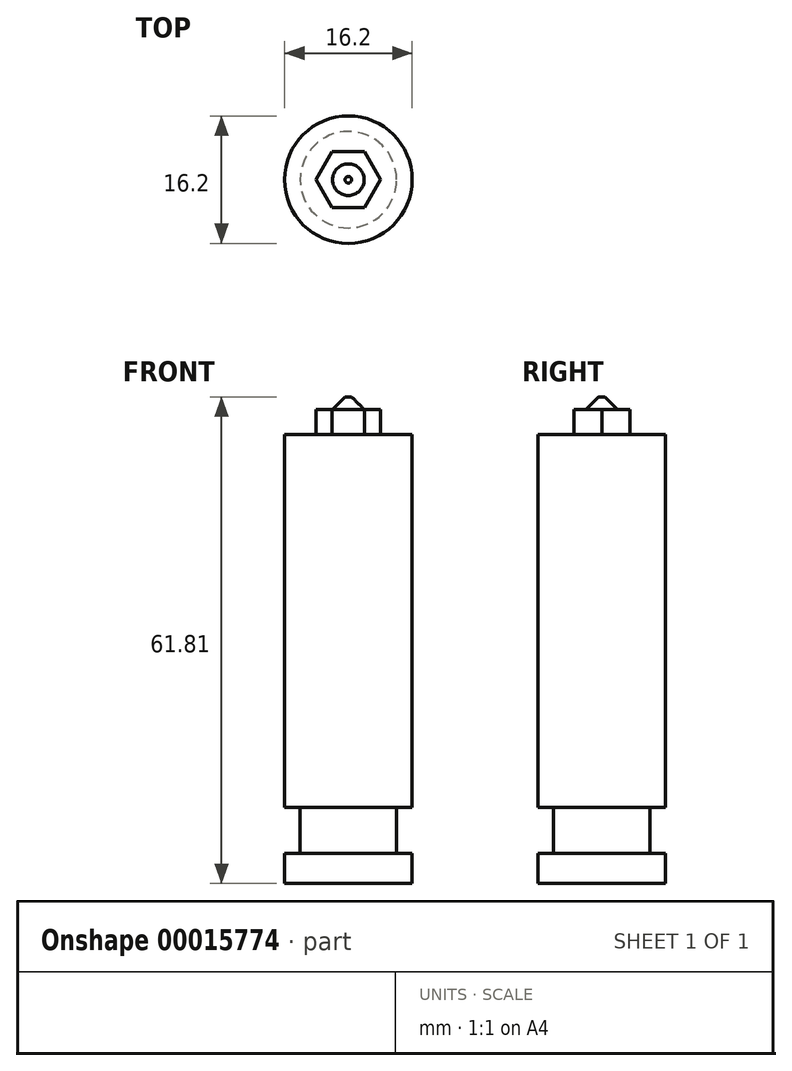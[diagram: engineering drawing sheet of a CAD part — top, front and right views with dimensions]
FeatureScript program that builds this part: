
annotation { "Feature Type Name" : "Feature", "Feature Type Description" : "" }
export const myFeature = defineFeature(function(context is Context, id is Id, definition is map)
    precondition{}
    {
        {
            var Q0;
            Q0=qCreatedBy(makeId("Top.planeOp"),FACE);
            var sketch = newSketch(context, id + "F0", { "sketchPlane" : qUnion([Q0])});
            skCircle(sketch, "E0", {"center": v(0, 0) * mm, "radius": 8.1 * mm});
            skSolve(sketch);
        }
        {
            var Q0;
            Q0 = qSketchRegion(id + "F0", true);
            extrude(context, id + "F1", {"entities" : qUnion([Q0]), "depth" : 3.8 * mm});
        }
        {
            var Q0;
            Q0=makeQuery(id+"F1.opExtrude","CAP_FACE",FACE,{"disambiguationData":[OSD([sQuery(id+"F0.wireOp",EDGE,"E0")])],"isStart":false});
            var sketch = newSketch(context, id + "F2", { "sketchPlane" : qUnion([Q0])});
            skCircle(sketch, "E1", {"center": v(0, 0) * mm, "radius": 6.12 * mm});
            skSolve(sketch);
        }
        {
            var Q0;
            Q0 = qSketchRegion(id + "F2", true);
            extrude(context, id + "F3", {"entities" : qUnion([Q0]), "operationType" : NewBodyOperationType.ADD, "depth" : 5.87 * mm});
        }
        {
            var Q0;
            Q0=makeQuery(id+"F3.opExtrude","CAP_FACE",FACE,{"disambiguationData":[OSD([sQuery(id+"F2.wireOp",EDGE,"E1")])],"isStart":false});
            var sketch = newSketch(context, id + "F4", { "sketchPlane" : qUnion([Q0])});
            skCircle(sketch, "E2", {"center": v(0, 0) * mm, "radius": 8.1 * mm});
            skSolve(sketch);
        }
        {
            var Q0;
            Q0 = qSketchRegion(id + "F4", true);
            extrude(context, id + "F5", {"entities" : qUnion([Q0]), "operationType" : NewBodyOperationType.ADD, "depth" : 47.37 * mm});
        }
        {
            var Q0;
            Q0=makeQuery(id+"F5.opExtrude","CAP_FACE",FACE,{"disambiguationData":[OSD([sQuery(id+"F4.wireOp",EDGE,"E2")])],"isStart":false});
            var sketch = newSketch(context, id + "F6", { "sketchPlane" : qUnion([Q0])});
            skCircle(sketch, "E3.cCircle", {"center": v(0, 0) * mm, "radius": 3.56 * mm, "construction": true});
            skLineSegment(sketch, "E3.0", {"start": v(2.05, -3.56) * mm, "end": v(-2.05, -3.56) * mm});
            skLineSegment(sketch, "E3.1", {"start": v(-2.05, -3.56) * mm, "end": v(-4.1, 0) * mm});
            skLineSegment(sketch, "E3.2", {"start": v(-4.1, 0) * mm, "end": v(-2.05, 3.56) * mm});
            skLineSegment(sketch, "E3.3", {"start": v(-2.05, 3.56) * mm, "end": v(2.05, 3.56) * mm});
            skLineSegment(sketch, "E3.4", {"start": v(2.05, 3.56) * mm, "end": v(4.1, 0) * mm});
            skLineSegment(sketch, "E3.5", {"start": v(4.1, 0) * mm, "end": v(2.05, -3.56) * mm});
            skPoint(sketch, "E3.0.midPoint", {"position": v(0, -3.56) * mm});
            skSolve(sketch);
        }
        {
            var Q0;
            Q0 = qSketchRegion(id + "F6", true);
            extrude(context, id + "F7", {"entities" : qUnion([Q0]), "operationType" : NewBodyOperationType.ADD, "depth" : 3.17 * mm});
        }
        {
            var Q0;
            Q0=makeQuery(id+"F7.opExtrude","CAP_FACE",FACE,{"disambiguationData":[OSD([sQuery(id+"F6.wireOp",EDGE,"E3.0"),sQuery(id+"F6.wireOp",EDGE,"E3.1"),sQuery(id+"F6.wireOp",EDGE,"E3.2"),sQuery(id+"F6.wireOp",EDGE,"E3.3"),sQuery(id+"F6.wireOp",EDGE,"E3.4"),sQuery(id+"F6.wireOp",EDGE,"E3.5")])],"isStart":false});
            var sketch = newSketch(context, id + "F8", { "sketchPlane" : qUnion([Q0])});
            skCircle(sketch, "E4", {"center": v(0, 0) * mm, "radius": 2 * mm});
            skSolve(sketch);
        }
        {
            var Q0;
            Q0 = qSketchRegion(id + "F8", true);
            extrude(context, id + "F9", {"entities" : qUnion([Q0]), "operationType" : NewBodyOperationType.ADD, "depth" : 1.59 * mm});
        }
        {
            var Q0;
            Q0=makeQuery(id+"F9.opExtrude","CAP_EDGE",EDGE,{"disambiguationData":[OSD([sQuery(id+"F8.wireOp",EDGE,"E4")])],"isStart":false});
            chamfer(context, id + "F10", {"entities" : qUnion([Q0]), "width" : 1.59 * mm, "tangentPropagation" : true});
        }
    });
